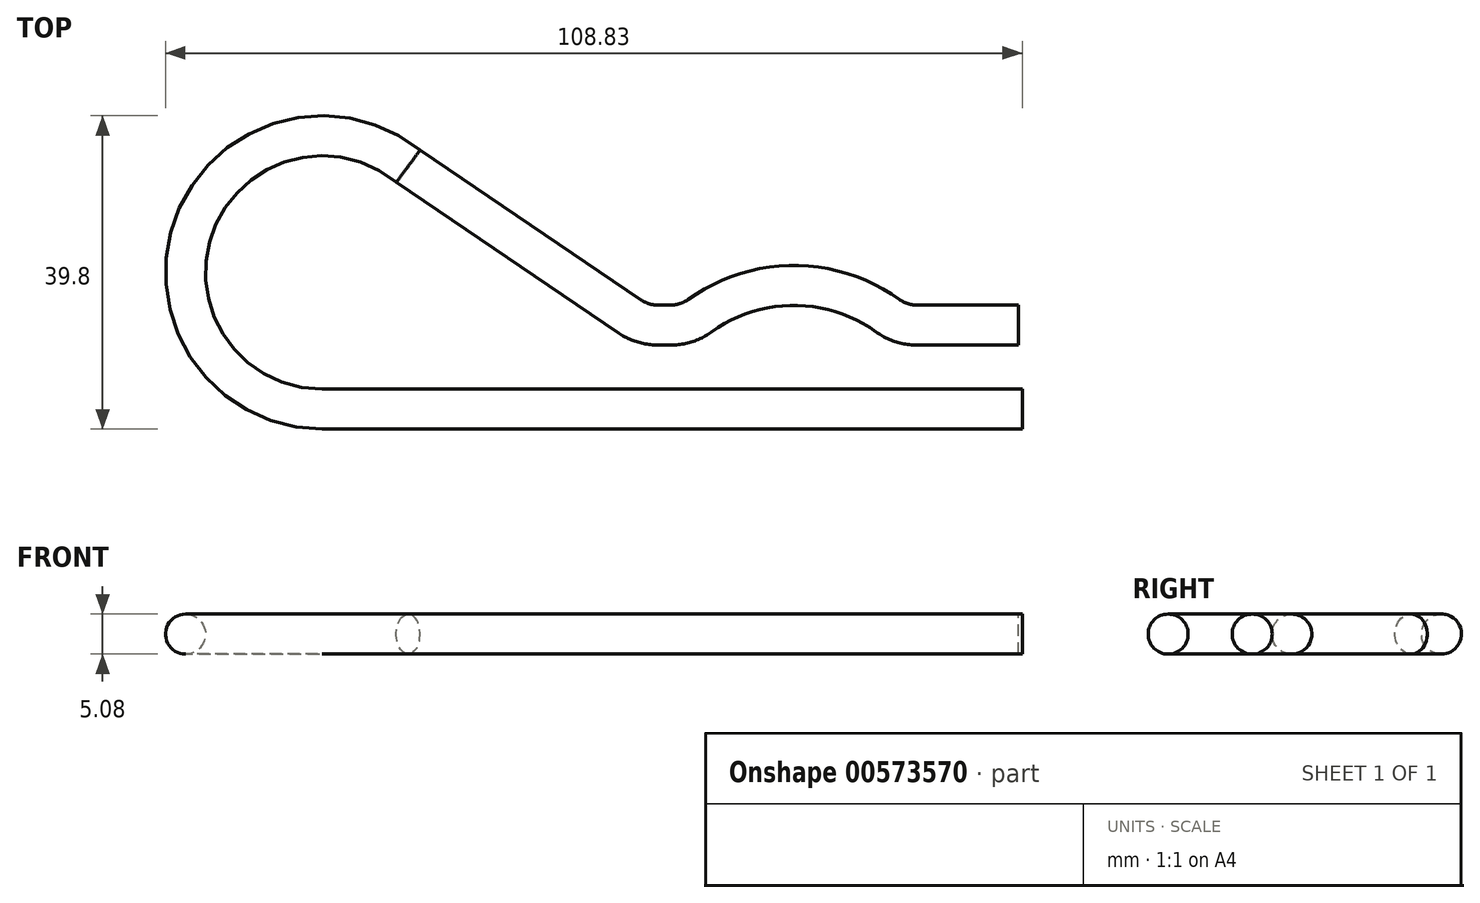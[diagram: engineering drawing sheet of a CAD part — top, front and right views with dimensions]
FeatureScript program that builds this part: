
annotation { "Feature Type Name" : "Feature", "Feature Type Description" : "" }
export const myFeature = defineFeature(function(context is Context, id is Id, definition is map)
    precondition{}
    {
        {
            var Q0;
            Q0=qCreatedBy(makeId("Top.planeOp"),FACE);
            var sketch = newSketch(context, id + "F0", { "sketchPlane" : qUnion([Q0])});
            skArc(sketch, "E0", {"start": v(-26.25, 30.86) * mm, "mid": v(-53.55, 23.16) * mm, "end": v(-37.18, 0) * mm});
            skLineSegment(sketch, "E1", {"start": v(-37.18, 0) * mm, "end": v(51.75, 0) * mm});
            skLineSegment(sketch, "E2", {"start": v(51.25, 10.68) * mm, "end": v(38.37, 10.68) * mm});
            skLineSegment(sketch, "E3", {"start": v(-26.25, 30.86) * mm, "end": v(1.9, 11.77) * mm});
            skArc(sketch, "E4", {"start": v(34.67, 11.87) * mm, "mid": v(22.73, 15.71) * mm, "end": v(10.8, 11.87) * mm});
            skLineSegment(sketch, "E5.trimOffspring", {"start": v(7.1, 10.68) * mm, "end": v(5.47, 10.68) * mm});
            skPoint(sketch, "E6.visualSharp", {"position": v(3.52, 10.68) * mm});
            skArc(sketch, "E6.filletArc", {"start": v(1.9, 11.77) * mm, "mid": v(3.6, 10.96) * mm, "end": v(5.47, 10.68) * mm});
            skPoint(sketch, "E7.visualSharp", {"position": v(9.3, 10.68) * mm});
            skArc(sketch, "E7.filletArc", {"start": v(7.1, 10.68) * mm, "mid": v(9.04, 10.98) * mm, "end": v(10.8, 11.87) * mm});
            skPoint(sketch, "E8.visualSharp", {"position": v(36.17, 10.68) * mm});
            skArc(sketch, "E8.filletArc", {"start": v(34.67, 11.87) * mm, "mid": v(36.43, 10.98) * mm, "end": v(38.37, 10.68) * mm});
            skPoint(sketch, "E9", {"position": v(0, 0) * mm});
            skSolve(sketch);
        }
        {
            var Q0;
            Q0=qCreatedBy(makeId("Right.planeOp"),FACE);
            var Q1;
            Q1 = qBodyType(qCreatedBy(id + "Fz3QdwD4PKHtZvS_0" ,EDGE), BodyType.WIRE);
            cPlane(context, id + "F1", {"entities" : qUnion([Q0, Q1]), "cplaneType" : CPlaneType.OFFSET, "offset" : 51.74 * mm, "width" : 152.4 * mm, "height" : 152.4 * mm});
        }
        {
            var Q0;
            Q0=qCreatedBy(id+"F1.planeOp",FACE);
            var sketch = newSketch(context, id + "F2", { "sketchPlane" : qUnion([Q0])});
            skCircle(sketch, "E10", {"center": v(0, 0) * mm, "radius": 2.54 * mm});
            skSolve(sketch);
        }
        {
            var Q0;
            Q0 = qSketchRegion(id + "F2", true);
            var Q1;
            Q1 = qConstructionFilter(qBodyType(qCreatedBy(id + "F0" ,EDGE), BodyType.WIRE), ConstructionObject.NO);
            sweep(context, id + "F3", {"profiles" : qUnion([Q0]), "path" : qUnion([Q1])});
        }
    });
